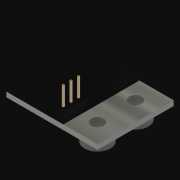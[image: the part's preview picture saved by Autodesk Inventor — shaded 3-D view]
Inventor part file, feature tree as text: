
AUTODESK INVENTOR PART (.ipt)
format: ipt  version: 2021 (Build 250183000, 183)  size: 130,048 bytes
history: native  units: in
note: dims shown in document units (in); Inventor stores cm internally (conversion verified against a paired STEP export)
features: extrude x1, other x1, imported_body x1
ambient origin geometry x8: Origin, YZ Plane, XZ Plane, XY Plane, X Axis, Y Axis, Z Axis, Center Point
bodies: Body1 (feature_tree)
feature tree (3):
  extrude  "Extrude6"  [1 undecoded]
  other  "276-2333-001 Rev21"
  imported_body  "Base1"
note: 1 required parameter value undecoded (feature->parameter linkage not recoverable at this tier; creation-order binding heuristic only, values carry confidence <= 0.55)
